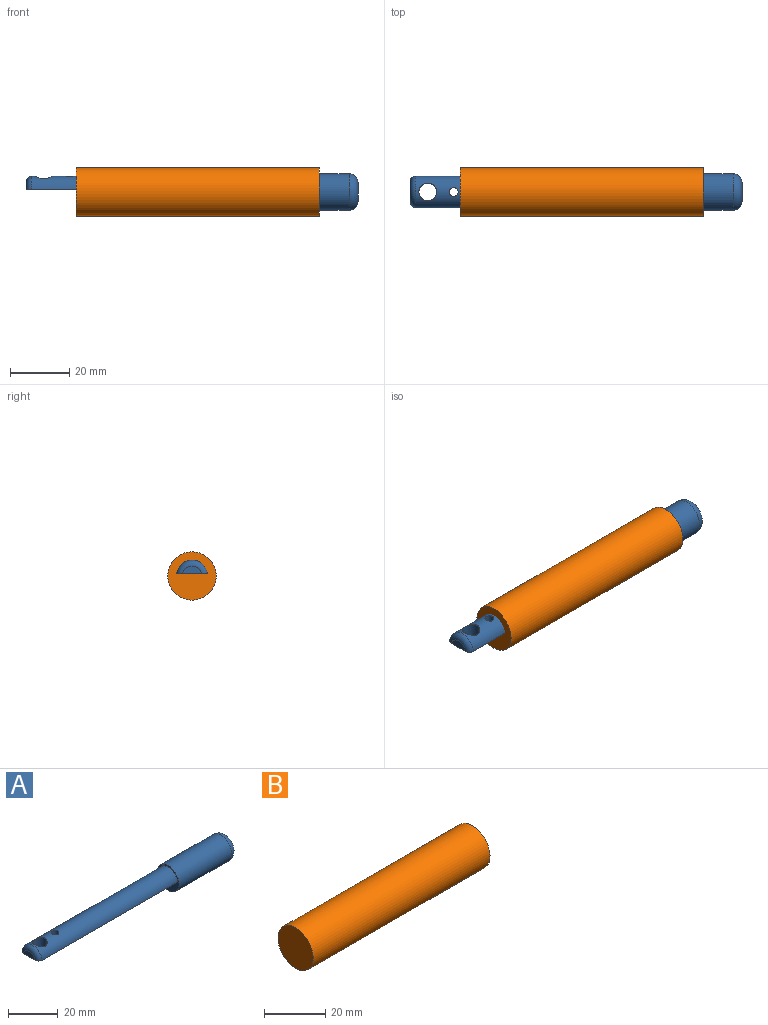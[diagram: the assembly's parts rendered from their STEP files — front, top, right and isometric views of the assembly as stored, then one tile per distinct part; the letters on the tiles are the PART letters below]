
ASSEMBLY  parts=2 mates=1
PART A: 12 faces, bbox 112x13.3x13.3 mm
  f0: cylinder r=5.35mm len=77mm, axis (1,0,0), area 1149.4mm2, adj f1,f5,f7,f10,f11
  f1: plane 12.3x12.3mm, normal (-1,0,0), area 86.9mm2, adj f0,f2,f5,f8
  f2: cylinder r=6.15mm len=30mm, axis (1,0,0), area 1159.2mm2, adj f1,f4
  f3: plane 6.3x6.3mm, normal (1,0,0), area 31.2mm2, adj f4
  f4: torus R=3.15mm, axis (1,0,0), area 149.8mm2, adj f2,f3
  f5: plane 79x10.61mm, normal (0,0,-1), area 591.2mm2, adj f0,f1,f6,f7,f8,f9,f10,f11
  f6: plane 6.55x2.65mm, normal (-1,0,0), area 13mm2, adj f5,f7
  f7: torus R=3.35mm, axis (-1,0,0), area 41.2mm2, adj f0,f5,f6
  f8: cylinder r=4mm len=35mm, axis (1,0,0), area 237.1mm2, adj f1,f5,f9
  f9: plane 5.99x1.35mm, normal (1,0,0), area 5.6mm2, adj f5,f8
  f10: cylinder r=3mm len=6mm, axis (0,0,-1), area 79.2mm2, adj f0,f5
  f11: cylinder r=1.5mm len=4.65mm, axis (0,0,-1), area 42.8mm2, adj f0,f5
PART B: 5 faces, bbox 82x16.3x16.3 mm
  f0: cylinder r=6.15mm len=55mm, axis (-1,0,0), area 2125.3mm2, adj f2,f4
  f1: cylinder r=8.15mm len=82mm, axis (-1,0,0), area 4199.1mm2, adj f2,f3
  f2: plane 16.3x16.3mm, normal (1,0,0), area 89.8mm2, adj f0,f1
  f3: plane 16.3x16.3mm, normal (-1,0,0), area 208.7mm2, adj f1
  f4: plane 12.3x12.3mm, normal (1,0,0), area 118.8mm2, adj f0
PLACE A at identity
PLACE B t=(-120,0,0)mm
MATE fastened B.f1 <-> A.f2  axis (1,0,0) through (-13,0,0)mm
